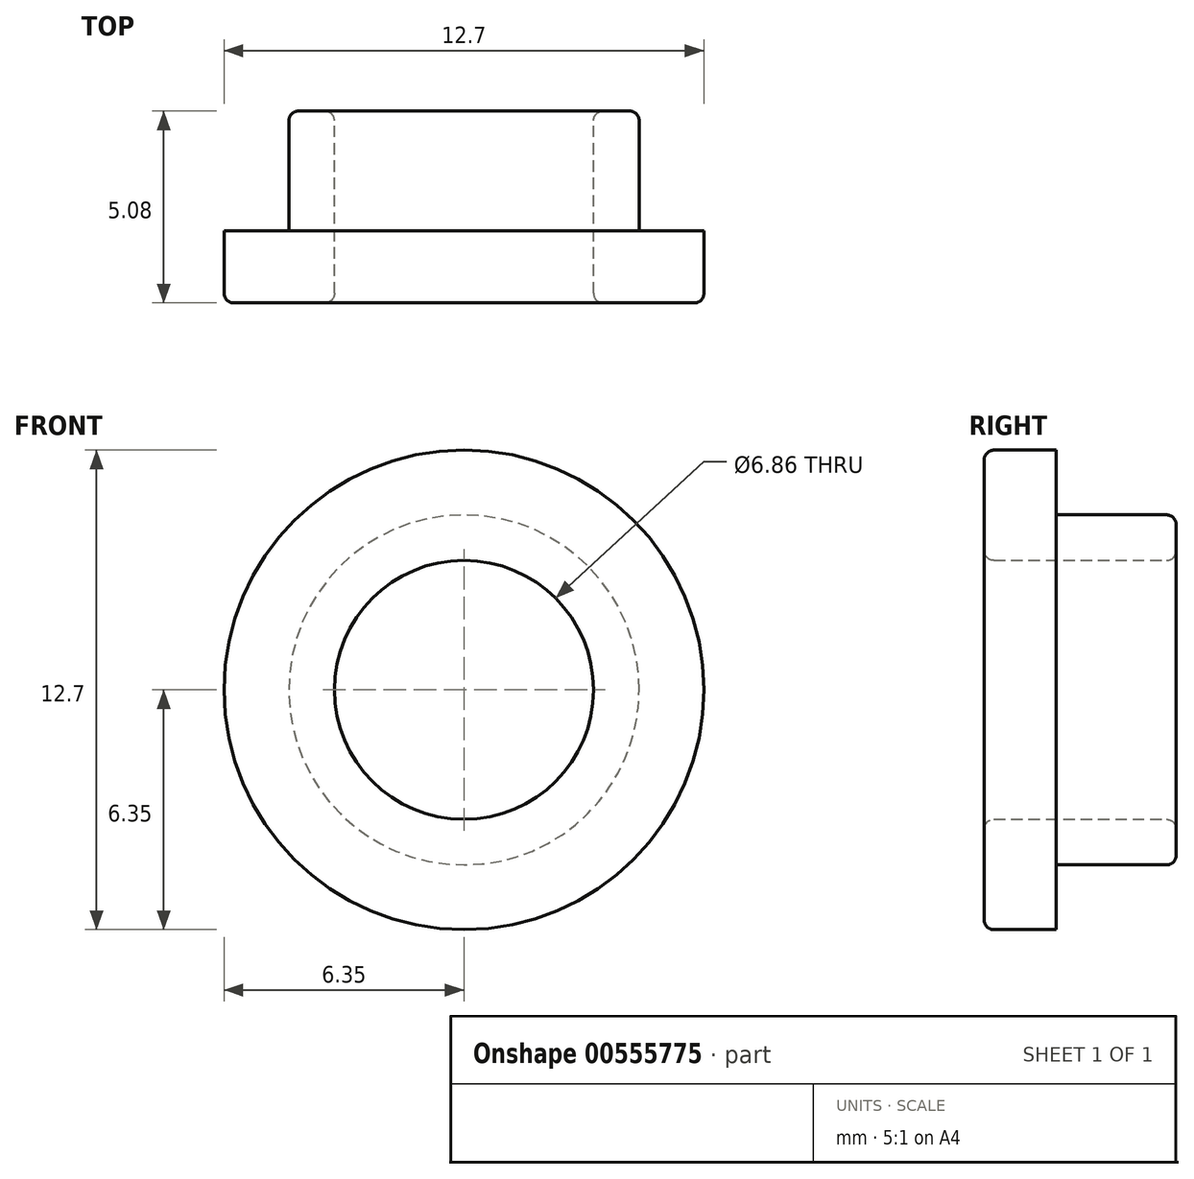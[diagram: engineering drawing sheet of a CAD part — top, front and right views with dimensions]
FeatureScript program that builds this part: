
annotation { "Feature Type Name" : "Feature", "Feature Type Description" : "" }
export const myFeature = defineFeature(function(context is Context, id is Id, definition is map)
    precondition{}
    {
        {
            var Q0;
            Q0=qCreatedBy(makeId("Front.planeOp"),FACE);
            var sketch = newSketch(context, id + "F0", { "sketchPlane" : qUnion([Q0])});
            skCircle(sketch, "E0", {"center": v(0, 0) * mm, "radius": 3.43 * mm});
            skCircle(sketch, "E1", {"center": v(0, 0) * mm, "radius": 4.64 * mm});
            skSolve(sketch);
        }
        {
            var Q0;
            Q0=makeQuery(id+"F0.imprint","IMPRINT",FACE,{"disambiguationData":[TD([[makeQuery(id+"F0.imprint","IMPRINT",EDGE,{"derivedFrom":sQuery(id+"F0.wireOp",EDGE,"E0")}),-1.0]])]});
            extrude(context, id + "F1", {"entities" : qUnion([Q0]), "depth" : 3.17 * mm, "offsetDistance" : 25.4 * mm});
        }
        {
            var Q0;
            Q0=makeQuery(id+"F1.opExtrude","CAP_FACE",FACE,{"disambiguationData":[OSD([sQuery(id+"F0.wireOp",EDGE,"E0"),sQuery(id+"F0.wireOp",EDGE,"E1")])],"isStart":false});
            var sketch = newSketch(context, id + "F2", { "sketchPlane" : qUnion([Q0])});
            skCircle(sketch, "E2", {"center": v(0, 0) * mm, "radius": 3.43 * mm});
            skCircle(sketch, "E3", {"center": v(0, 0) * mm, "radius": 6.35 * mm});
            skSolve(sketch);
        }
        {
            var Q0;
            Q0=makeQuery(id+"F2.imprint","IMPRINT",FACE,{"disambiguationData":[TD([[makeQuery(id+"F2.imprint","IMPRINT",EDGE,{"derivedFrom":sQuery(id+"F2.wireOp",EDGE,"E2")}),-1.0]])]});
            var Q1;
            Q1=makeQuery(id+"F2.imprint","IMPRINT",FACE,{"disambiguationData":[TD([[makeQuery(id+"F2.imprint","IMPRINT",EDGE,{"derivedFrom":sQuery(id+"F2.wireOp",EDGE,"E3")}),1.0]])]});
            extrude(context, id + "F3", {"entities" : qUnion([Q0, Q1]), "operationType" : NewBodyOperationType.ADD, "depth" : 1.9 * mm, "offsetDistance" : 25.4 * mm});
        }
        {
            var Q0;
            Q0=makeQuery(id+"F3.opExtrude","CAP_EDGE",EDGE,{"disambiguationData":[OSD([sQuery(id+"F2.wireOp",EDGE,"E3")])],"isStart":false});
            var Q1;
            Q1=makeQuery(id+"F3.opExtrude","CAP_EDGE",EDGE,{"disambiguationData":[OSD([sQuery(id+"F2.wireOp",EDGE,"E2")])],"isStart":false});
            var Q2;
            Q2=makeQuery(id+"F1.opExtrude","CAP_EDGE",EDGE,{"disambiguationData":[OSD([sQuery(id+"F0.wireOp",EDGE,"E1")])],"isStart":true});
            var Q3;
            Q3=makeQuery(id+"F1.opExtrude","CAP_EDGE",EDGE,{"disambiguationData":[OSD([sQuery(id+"F0.wireOp",EDGE,"E0")])],"isStart":true});
            fillet(context, id + "F4", {"entities" : qUnion([Q0, Q1, Q2, Q3]), "radius" : 0.25 * mm, "tangentPropagation" : true, "allowEdgeOverflow" : false});
        }
    });
